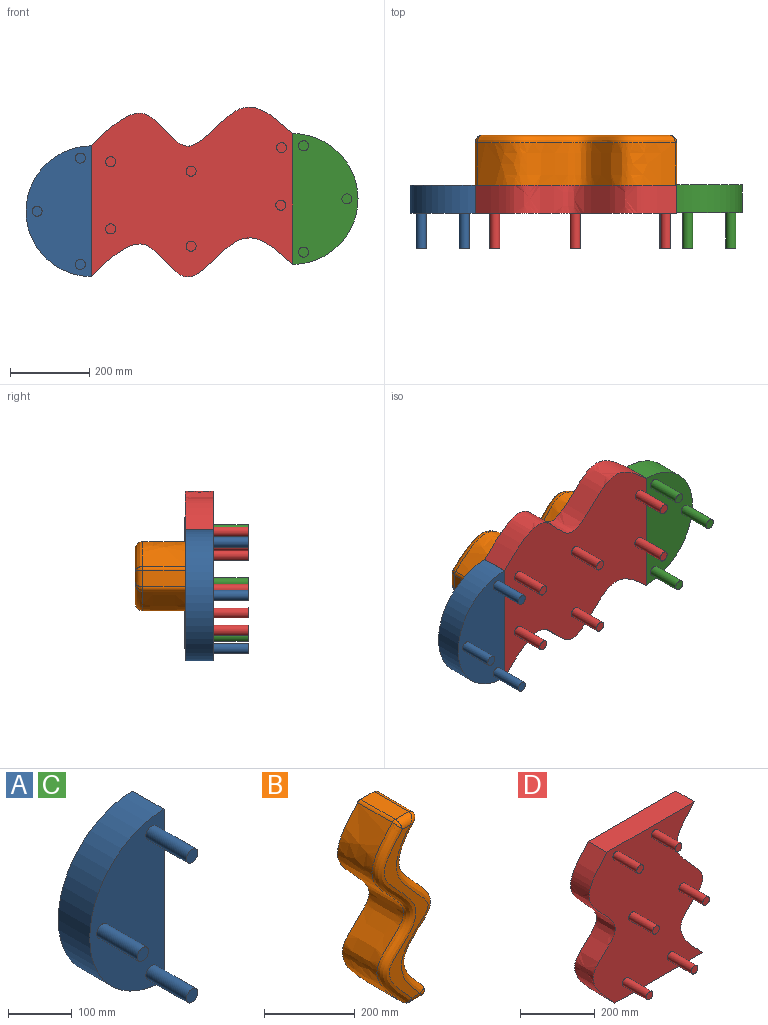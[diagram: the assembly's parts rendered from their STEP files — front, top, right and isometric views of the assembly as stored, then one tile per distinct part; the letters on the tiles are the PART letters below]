
ASSEMBLY  parts=4 mates=3
PART A: 16 faces, bbox 165.1x160x330.2 mm
  f0: plane 330.2x70mm, normal (1,0,0), area 19952.5mm2, adj f1,f2,f3,f10,f12,f14
  f1: cylinder r=165.1mm len=330.2mm, axis (0,1,0), area 36307.4mm2, adj f0,f2,f3
  f2: plane 330.2x165.1mm, normal (0,-1,0), area 41296.7mm2, adj f0,f1,f4,f6,f8
  f3: plane 330.2x165.1mm, normal (0,1,0), area 42816.8mm2, adj f0,f1
  f4: cylinder r=12.7mm len=90mm, axis (0,1,0), area 7181.7mm2, adj f2,f5
  f5: plane 25.4x25.4mm, normal (0,-1,0), area 506.7mm2, adj f4
  f6: cylinder r=12.7mm len=90mm, axis (0,1,0), area 7181.7mm2, adj f2,f7
  f7: plane 25.4x25.4mm, normal (0,-1,0), area 506.7mm2, adj f6
  f8: cylinder r=12.7mm len=90mm, axis (0,1,0), area 7181.7mm2, adj f2,f9
  f9: plane 25.4x25.4mm, normal (0,-1,0), area 506.7mm2, adj f8
  f10: cylinder r=18.39mm len=36.79mm, axis (-1,0,0), area 2.9mm2, adj f0,f11
  f11: plane 36.79x36.79mm, normal (1,0,0), area 1063mm2, adj f10
  f12: cylinder r=18.72mm len=37.44mm, axis (-1,0,0), area 3mm2, adj f0,f13
  f13: plane 37.44x37.44mm, normal (1,0,0), area 1100.9mm2, adj f12
  f14: cylinder r=17.82mm len=35.64mm, axis (-1,0,0), area 2.8mm2, adj f0,f15
  f15: plane 35.64x35.64mm, normal (1,0,0), area 997.7mm2, adj f14
PART B: 18 faces, bbox 189.3x128.6x509.2 mm
  f0: extruded ~465.46x107.95mm, area 60745.6mm2, adj f5,f6,f10,f12
  f1: plane 107.95x41.93mm, normal (0,0,1), area 4526.3mm2, adj f5,f7,f12,f14
  f2: extruded ~500.03x107.95mm, area 65875.1mm2, adj f5,f9,f14,f16
  f3: plane 107.95x41mm, normal (0,0,-1), area 4425.7mm2, adj f5,f8,f10,f16
  f4: plane 469.94x136.88mm, normal (0,-1,0), area 14135.7mm2, adj f6,f7,f8,f9
  f5: plane 508x189.31mm, normal (0,1,0), area 38334.4mm2, adj f0,f1,f2,f3,f10,f12,f14,f16
  f6: bspline ~507.63x117.83mm, area 16790mm2, adj f0,f4,f11,f13
  f7: cylinder r=19.05mm len=41.93mm, axis (1,0,0), area 1005mm2, adj f1,f4,f13,f15
  f8: cylinder r=19.05mm len=41mm, axis (-1,0,0), area 968.3mm2, adj f3,f4,f11,f17
  f9: bspline ~507.79x117.85mm, area 17854.3mm2, adj f2,f4,f15,f17
  f10: cylinder r=12.7mm len=107.95mm, axis (0,1,0), area 3191.6mm2, adj f0,f3,f5,f11
  f11: bspline ~44.12x23.93mm, area 506.4mm2, adj f6,f8,f10
  f12: cylinder r=12.7mm len=107.95mm, axis (0,1,0), area 3146.9mm2, adj f0,f1,f5,f13
  f13: bspline ~42.14x26.94mm, area 493.2mm2, adj f6,f7,f12
  f14: cylinder r=12.7mm len=107.95mm, axis (0,1,0), area 1134.6mm2, adj f1,f2,f5,f15
  f15: bspline ~19.91x19.06mm, area 132.5mm2, adj f7,f9,f14
  f16: cylinder r=12.7mm len=107.95mm, axis (0,1,0), area 1098.6mm2, adj f2,f3,f5,f17
  f17: bspline ~19.76x19.05mm, area 127.8mm2, adj f8,f9,f16
PART C: same geometry as A
PART D: 18 faces, bbox 443.3x160.2x508 mm
  f0: extruded ~508x98.33mm, area 43632.7mm2, adj f1,f3,f4,f5
  f1: plane 330.2x70.23mm, normal (0,0,1), area 23190.3mm2, adj f0,f2,f4,f5
  f2: extruded ~508x98.33mm, area 43632.7mm2, adj f1,f3,f4,f5
  f3: plane 330.2x70.23mm, normal (0,0,-1), area 23190.3mm2, adj f0,f2,f4,f5
  f4: plane 508x443.29mm, normal (0,-1,0), area 164701mm2, adj f0,f1,f2,f3,f6,f8,f10,f12
  f5: plane 508x443.29mm, normal (0,1,0), area 167741.3mm2, adj f0,f1,f2,f3
  f6: cylinder r=12.7mm len=90mm, axis (0,1,0), area 7181.7mm2, adj f4,f7
  f7: plane 25.4x25.4mm, normal (0,-1,0), area 506.7mm2, adj f6
  f8: cylinder r=12.7mm len=90mm, axis (0,1,0), area 7181.7mm2, adj f4,f9
  f9: plane 25.4x25.4mm, normal (0,-1,0), area 506.7mm2, adj f8
  f10: cylinder r=12.7mm len=90mm, axis (0,1,0), area 7181.7mm2, adj f4,f11
  f11: plane 25.4x25.4mm, normal (0,-1,0), area 506.7mm2, adj f10
  f12: cylinder r=12.7mm len=90mm, axis (0,1,0), area 7181.7mm2, adj f4,f13
  f13: plane 25.4x25.4mm, normal (0,-1,0), area 506.7mm2, adj f12
  f14: cylinder r=12.7mm len=90mm, axis (0,1,0), area 7181.7mm2, adj f4,f15
  f15: plane 25.4x25.4mm, normal (0,-1,0), area 506.7mm2, adj f14
  f16: cylinder r=12.7mm len=90mm, axis (0,1,0), area 7181.7mm2, adj f4,f17
  f17: plane 25.4x25.4mm, normal (0,-1,0), area 506.7mm2, adj f16
PLACE A t=(-785.99,22.22,250.36)mm
PLACE B rot(axis=(0.71,0,-0.71),180deg) t=(-538.17,22.58,239.91)mm
PLACE C rot(axis=(0,-1,0),180deg) t=(-277.97,23.99,281.34)mm
PLACE D rot(axis=(0,1,0),90deg) t=(-525.74,22.58,367.51)mm
MATE fastened D.f3 <-> A.f0  axis (-1,0,0) through (-785.99,-12.53,250.79)mm
MATE fastened B.f5 <-> D.f5  axis (0,-1,0) through (-531.99,22.58,303.89)mm
MATE fastened C.f10 <-> D.f1  axis (-1,0,0) through (-277.99,-12.53,281.34)mm
